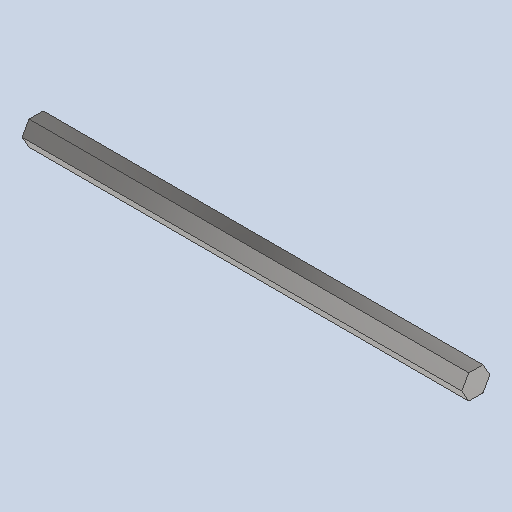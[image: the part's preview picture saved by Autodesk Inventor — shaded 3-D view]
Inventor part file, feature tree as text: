
AUTODESK INVENTOR PART (.ipt)
format: ipt  version: 2023 (Build 270158000, 158)  size: 90,112 bytes
history: native  units: in
note: dims shown in document units (in); Inventor stores cm internally (conversion verified against a paired STEP export)
features: other x3, sketch x1
ambient origin geometry x8: Origin, YZ Plane, XZ Plane, XY Plane, X Axis, Y Axis, Z Axis, Center Point
bodies: Solid1 (feature_tree)
feature tree (4):
  other  "9in-0.5inHexAxel_MIR1.ipt"
  other  "Solid1::9in-0.5inHexAxel_MIR1.ipt"
  other  "TaggingFeature1"
  sketch  "Sketch1"  dims[d0=0.3937in]
